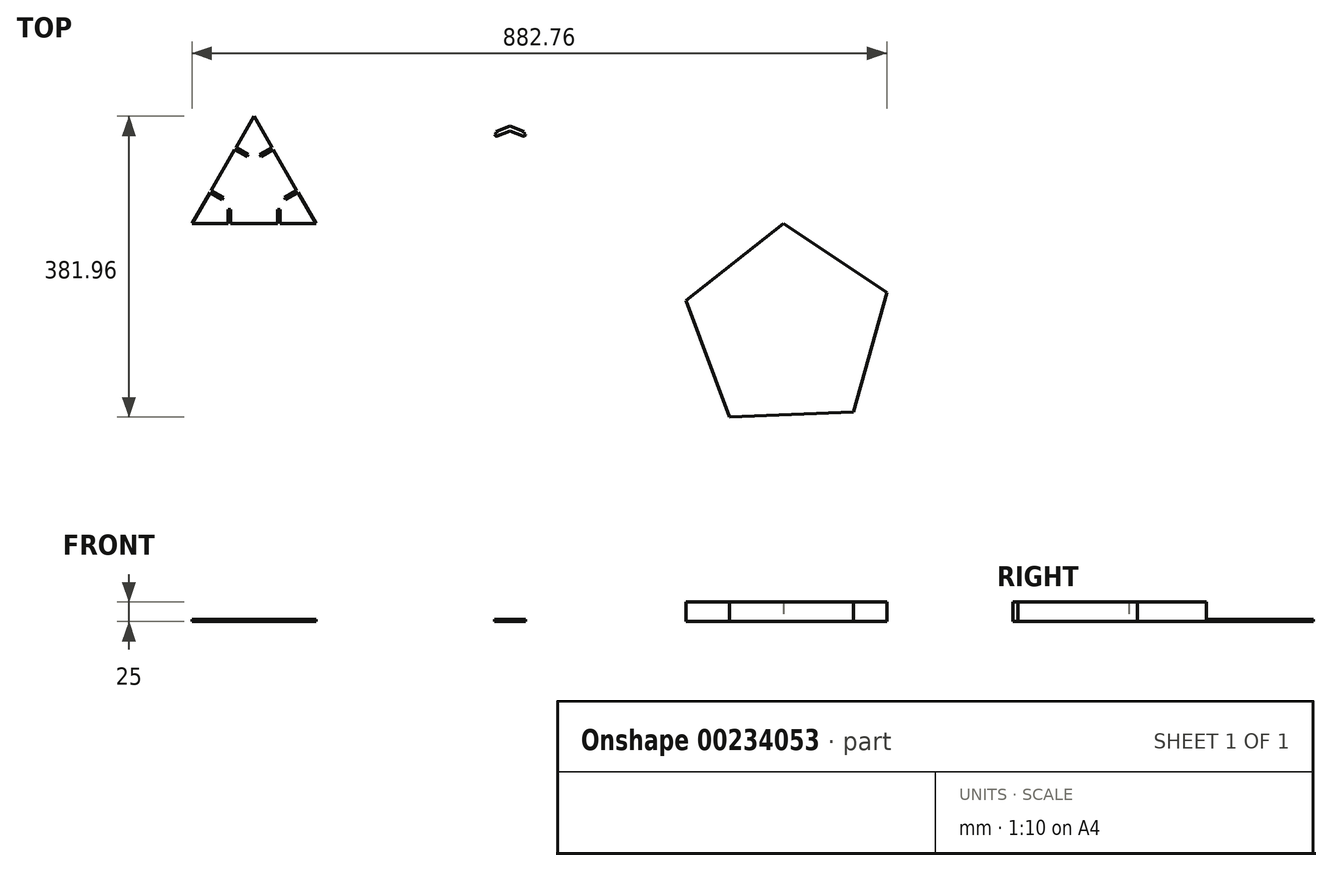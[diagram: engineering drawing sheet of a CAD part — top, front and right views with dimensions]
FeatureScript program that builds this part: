
annotation { "Feature Type Name" : "Feature", "Feature Type Description" : "" }
export const myFeature = defineFeature(function(context is Context, id is Id, definition is map)
    precondition{}
    {
        {
            var Q0;
            Q0=qCreatedBy(makeId("Top.planeOp"),FACE);
            var sketch = newSketch(context, id + "F0", { "sketchPlane" : qUnion([Q0])});
            skLineSegment(sketch, "E0", {"start": v(0, 0) * mm, "end": v(78.83, 136.53) * mm});
            skLineSegment(sketch, "E1", {"start": v(78.83, 136.53) * mm, "end": v(157.65, 0) * mm});
            skLineSegment(sketch, "E2", {"start": v(157.65, 0) * mm, "end": v(0, 0) * mm});
            skLineSegment(sketch, "E3", {"start": v(78.83, 136.53) * mm, "end": v(236.47, 136.53) * mm});
            skLineSegment(sketch, "E4", {"start": v(236.48, 136.53) * mm, "end": v(157.65, 0) * mm});
            skLineSegment(sketch, "E5", {"start": v(78.83, 136.53) * mm, "end": v(157.65, 273.06) * mm});
            skLineSegment(sketch, "E6", {"start": v(157.65, 273.06) * mm, "end": v(236.47, 136.53) * mm});
            skLineSegment(sketch, "E7.1.0", {"start": v(157.65, 0) * mm, "end": v(78.83, -136.53) * mm});
            skLineSegment(sketch, "E7.1.1", {"start": v(0, 0) * mm, "end": v(157.65, 0) * mm});
            skLineSegment(sketch, "E7.1.2", {"start": v(78.83, -136.53) * mm, "end": v(0, 0) * mm});
            skLineSegment(sketch, "E7.1.3", {"start": v(157.65, 0) * mm, "end": v(315.3, 0) * mm});
            skLineSegment(sketch, "E7.1.4", {"start": v(236.48, -136.53) * mm, "end": v(78.83, -136.53) * mm});
            skLineSegment(sketch, "E7.1.5", {"start": v(157.65, 0) * mm, "end": v(236.48, -136.53) * mm});
            skLineSegment(sketch, "E7.1.6", {"start": v(315.3, 0) * mm, "end": v(236.47, -136.53) * mm});
            skLineSegment(sketch, "E7.2.0", {"start": v(78.83, -136.53) * mm, "end": v(-78.82, -136.53) * mm});
            skLineSegment(sketch, "E7.2.1", {"start": v(0, 0) * mm, "end": v(78.83, -136.53) * mm});
            skLineSegment(sketch, "E7.2.2", {"start": v(-78.82, -136.53) * mm, "end": v(0, 0) * mm});
            skLineSegment(sketch, "E7.2.3", {"start": v(78.83, -136.53) * mm, "end": v(157.65, -273.06) * mm});
            skLineSegment(sketch, "E7.2.4", {"start": v(0, -273.06) * mm, "end": v(-78.83, -136.53) * mm});
            skLineSegment(sketch, "E7.2.5", {"start": v(78.83, -136.53) * mm, "end": v(0, -273.06) * mm});
            skLineSegment(sketch, "E7.2.6", {"start": v(157.65, -273.06) * mm, "end": v(0, -273.06) * mm});
            skLineSegment(sketch, "E7.3.0", {"start": v(-78.83, -136.53) * mm, "end": v(-157.65, 0) * mm});
            skLineSegment(sketch, "E7.3.1", {"start": v(0, 0) * mm, "end": v(-78.83, -136.53) * mm});
            skLineSegment(sketch, "E7.3.2", {"start": v(-157.65, 0) * mm, "end": v(0, 0) * mm});
            skLineSegment(sketch, "E7.3.3", {"start": v(-78.83, -136.53) * mm, "end": v(-157.65, -273.06) * mm});
            skLineSegment(sketch, "E7.3.4", {"start": v(-236.48, -136.53) * mm, "end": v(-157.65, 0) * mm});
            skLineSegment(sketch, "E7.3.5", {"start": v(-78.83, -136.53) * mm, "end": v(-236.47, -136.53) * mm});
            skLineSegment(sketch, "E7.3.6", {"start": v(-157.65, -273.06) * mm, "end": v(-236.47, -136.53) * mm});
            skLineSegment(sketch, "E7.4.0", {"start": v(-157.65, 0) * mm, "end": v(-78.83, 136.53) * mm});
            skLineSegment(sketch, "E7.4.1", {"start": v(0, 0) * mm, "end": v(-157.65, 0) * mm});
            skLineSegment(sketch, "E7.4.2", {"start": v(-78.83, 136.53) * mm, "end": v(0, 0) * mm});
            skLineSegment(sketch, "E7.4.3", {"start": v(-157.65, 0) * mm, "end": v(-315.3, 0) * mm});
            skLineSegment(sketch, "E7.4.4", {"start": v(-236.48, 136.53) * mm, "end": v(-78.83, 136.53) * mm});
            skLineSegment(sketch, "E7.4.5", {"start": v(-157.65, 0) * mm, "end": v(-236.48, 136.53) * mm});
            skLineSegment(sketch, "E7.4.6", {"start": v(-315.3, 0) * mm, "end": v(-236.47, 136.53) * mm});
            skPoint(sketch, "E7.center", {"position": v(0, 0) * mm});
            skLineSegment(sketch, "E7.anchor1", {"start": v(0, 0) * mm, "end": v(157.65, 0) * mm, "construction": true});
            skLineSegment(sketch, "E7.anchor2", {"start": v(0, 0) * mm, "end": v(-78.83, 136.53) * mm, "construction": true});
            skSolve(sketch);
        }
        {
            var Q0;
            Q0=qCreatedBy(makeId("Top.planeOp"),FACE);
            var sketch = newSketch(context, id + "F1", { "sketchPlane" : qUnion([Q0])});
            skLineSegment(sketch, "E8.0", {"start": v(0, 0) * mm, "end": v(78.83, 136.53) * mm});
            skLineSegment(sketch, "E8.1", {"start": v(78.83, 136.53) * mm, "end": v(157.65, 273.06) * mm});
            skLineSegment(sketch, "E8.2", {"start": v(157.65, 273.06) * mm, "end": v(236.47, 136.53) * mm});
            skLineSegment(sketch, "E8.3", {"start": v(236.48, 136.53) * mm, "end": v(157.65, 0) * mm});
            skLineSegment(sketch, "E8.4", {"start": v(157.65, 0) * mm, "end": v(315.3, 0) * mm});
            skLineSegment(sketch, "E9.0", {"start": v(315.3, 0) * mm, "end": v(236.47, -136.53) * mm});
            skLineSegment(sketch, "E10.0", {"start": v(236.48, -136.53) * mm, "end": v(78.83, -136.53) * mm});
            skLineSegment(sketch, "E11.0", {"start": v(78.83, -136.53) * mm, "end": v(157.65, -273.06) * mm});
            skLineSegment(sketch, "E12.0", {"start": v(157.65, -273.06) * mm, "end": v(0, -273.06) * mm});
            skLineSegment(sketch, "E13.0", {"start": v(0, -273.06) * mm, "end": v(-78.83, -136.53) * mm});
            skLineSegment(sketch, "E14.0", {"start": v(-78.83, -136.53) * mm, "end": v(-157.65, -273.06) * mm});
            skLineSegment(sketch, "E15.0", {"start": v(-157.65, -273.06) * mm, "end": v(-236.47, -136.53) * mm});
            skLineSegment(sketch, "E16.0", {"start": v(-236.48, -136.53) * mm, "end": v(-157.65, 0) * mm});
            skLineSegment(sketch, "E17.0", {"start": v(-157.65, 0) * mm, "end": v(-315.3, 0) * mm});
            skLineSegment(sketch, "E18.0", {"start": v(-315.3, 0) * mm, "end": v(-236.47, 136.53) * mm});
            skLineSegment(sketch, "E19.0", {"start": v(-236.48, 136.53) * mm, "end": v(-78.83, 136.53) * mm});
            skLineSegment(sketch, "E20.0", {"start": v(-78.83, 136.53) * mm, "end": v(0, 0) * mm});
            skSolve(sketch);
        }
        {
            var Q0;
            Q0=makeQuery(id+"F0.imprint","IMPRINT",FACE,{"disambiguationData":[TD([[makeQuery(id+"F0.imprint","IMPRINT",EDGE,{"derivedFrom":sQuery(id+"F0.wireOp",EDGE,"E0")}),-1.0]])]});
            extrude(context, id + "F2", {"entities" : qUnion([Q0]), "depth" : 3 * mm});
        }
        {
            var Q0;
            Q0=qCreatedBy(makeId("Top.planeOp"),FACE);
            var sketch = newSketch(context, id + "F3", { "sketchPlane" : qUnion([Q0])});
            skCircle(sketch, "E21.cCircle", {"center": v(757.04, -133.78) * mm, "radius": 108.5 * mm, "construction": true});
            skLineSegment(sketch, "E21.0", {"start": v(882.76, -87.12) * mm, "end": v(840.27, -238.93) * mm});
            skLineSegment(sketch, "E21.1", {"start": v(840.27, -238.93) * mm, "end": v(682.76, -245.43) * mm});
            skLineSegment(sketch, "E21.2", {"start": v(682.76, -245.43) * mm, "end": v(627.9, -97.64) * mm});
            skLineSegment(sketch, "E21.3", {"start": v(627.9, -97.64) * mm, "end": v(751.5, 0.2) * mm});
            skLineSegment(sketch, "E21.4", {"start": v(751.5, 0.2) * mm, "end": v(882.76, -87.12) * mm});
            skPoint(sketch, "E21.0.midPoint", {"position": v(861.52, -163.02) * mm});
            skSolve(sketch);
        }
        {
            var Q0;
            Q0 = qSketchRegion(id + "F3", true);
            extrude(context, id + "F4", {"entities" : qUnion([Q0]), "depth" : 25 * mm});
        }
        {
            var Q0;
            Q0=makeQuery(id+"F2.opExtrude","CAP_FACE",FACE,{"disambiguationData":[OSD([sQuery(id+"F0.wireOp",EDGE,"E0"),sQuery(id+"F0.wireOp",EDGE,"E1"),sQuery(id+"F0.wireOp",EDGE,"E7.1.1")])],"isStart":false});
            var sketch = newSketch(context, id + "F5", { "sketchPlane" : qUnion([Q0])});
            skLineSegment(sketch, "E22.0", {"start": v(0, 0) * mm, "end": v(78.83, 136.53) * mm, "construction": true});
            skLineSegment(sketch, "E23.0", {"start": v(78.83, 136.53) * mm, "end": v(157.65, 0) * mm, "construction": true});
            skPoint(sketch, "E24.0", {"position": v(78.83, 0) * mm});
            skLineSegment(sketch, "E25.0", {"start": v(0, 0) * mm, "end": v(157.65, 0) * mm, "construction": true});
            skPoint(sketch, "E26", {"position": v(39.41, 68.26) * mm});
            skPoint(sketch, "E27", {"position": v(118.24, 68.26) * mm});
            skLineSegment(sketch, "E28", {"start": v(48.83, 0) * mm, "end": v(48.83, 18) * mm});
            skLineSegment(sketch, "E29", {"start": v(48.83, 18) * mm, "end": v(45.83, 18) * mm});
            skLineSegment(sketch, "E30", {"start": v(45.83, 18) * mm, "end": v(45.83, 0) * mm});
            skLineSegment(sketch, "E31", {"start": v(45.83, 0) * mm, "end": v(48.83, 0) * mm});
            skLineSegment(sketch, "E32", {"start": v(111.83, 0) * mm, "end": v(111.83, 18) * mm});
            skLineSegment(sketch, "E33", {"start": v(111.83, 18) * mm, "end": v(108.83, 18) * mm});
            skLineSegment(sketch, "E34", {"start": v(108.83, 18) * mm, "end": v(108.83, 0) * mm});
            skLineSegment(sketch, "E35", {"start": v(108.83, 0) * mm, "end": v(111.83, 0) * mm});
            skLineSegment(sketch, "E36", {"start": v(40, 33.28) * mm, "end": v(24.41, 42.28) * mm});
            skLineSegment(sketch, "E37", {"start": v(24.41, 42.28) * mm, "end": v(22.91, 39.69) * mm});
            skLineSegment(sketch, "E38", {"start": v(22.91, 39.69) * mm, "end": v(38.5, 30.69) * mm});
            skLineSegment(sketch, "E39", {"start": v(38.5, 30.69) * mm, "end": v(40, 33.28) * mm});
            skLineSegment(sketch, "E40", {"start": v(71.5, 87.84) * mm, "end": v(55.91, 96.84) * mm});
            skLineSegment(sketch, "E41", {"start": v(55.91, 96.84) * mm, "end": v(54.41, 94.25) * mm});
            skLineSegment(sketch, "E42", {"start": v(54.41, 94.25) * mm, "end": v(70, 85.25) * mm});
            skLineSegment(sketch, "E43", {"start": v(70, 85.25) * mm, "end": v(71.5, 87.84) * mm});
            skLineSegment(sketch, "E44", {"start": v(101.74, 96.84) * mm, "end": v(86.15, 87.84) * mm});
            skLineSegment(sketch, "E45", {"start": v(86.15, 87.84) * mm, "end": v(87.65, 85.25) * mm});
            skLineSegment(sketch, "E46", {"start": v(87.65, 85.25) * mm, "end": v(103.24, 94.25) * mm});
            skLineSegment(sketch, "E47", {"start": v(103.24, 94.25) * mm, "end": v(101.74, 96.84) * mm});
            skLineSegment(sketch, "E48", {"start": v(133.24, 42.28) * mm, "end": v(117.65, 33.28) * mm});
            skLineSegment(sketch, "E49", {"start": v(117.65, 33.28) * mm, "end": v(119.15, 30.69) * mm});
            skLineSegment(sketch, "E50", {"start": v(119.15, 30.69) * mm, "end": v(134.74, 39.69) * mm});
            skLineSegment(sketch, "E51", {"start": v(134.74, 39.69) * mm, "end": v(133.24, 42.28) * mm});
            skSolve(sketch);
        }
        {
            var Q0;
            Q0 = qSketchRegion(id + "F5", true);
            extrude(context, id + "F6", {"entities" : qUnion([Q0]), "operationType" : NewBodyOperationType.REMOVE, "oppositeDirection" : true, "depth" : 25 * mm});
        }
        {
            var Q0;
            Q0=qCreatedBy(makeId("Top.planeOp"),FACE);
            var sketch = newSketch(context, id + "F7", { "sketchPlane" : qUnion([Q0])});
            skLineSegment(sketch, "E52", {"start": v(404.23, 132.2) * mm, "end": v(404.23, 110.87) * mm, "construction": true});
            skLineSegment(sketch, "E53", {"start": v(404.23, 124.16) * mm, "end": v(386.35, 117.33) * mm});
            skLineSegment(sketch, "E54", {"start": v(386.35, 117.33) * mm, "end": v(387.42, 114.53) * mm});
            skLineSegment(sketch, "E55", {"start": v(387.42, 114.53) * mm, "end": v(384.62, 113.46) * mm});
            skLineSegment(sketch, "E56", {"start": v(384.62, 113.46) * mm, "end": v(384.97, 112.52) * mm});
            skLineSegment(sketch, "E57", {"start": v(387.56, 111.37) * mm, "end": v(404.23, 117.74) * mm});
            skLineSegment(sketch, "E58", {"start": v(387.42, 114.53) * mm, "end": v(404.23, 120.95) * mm, "construction": true});
            skPoint(sketch, "E59.visualSharp", {"position": v(385.69, 110.66) * mm});
            skArc(sketch, "E59.filletArc", {"start": v(384.97, 112.52) * mm, "mid": v(386.03, 111.41) * mm, "end": v(387.56, 111.37) * mm});
            skLineSegment(sketch, "E60.MirrorCS", {"start": v(423.85, 113.46) * mm, "end": v(423.5, 112.52) * mm});
            skArc(sketch, "E61.MirrorCS", {"start": v(423.5, 112.52) * mm, "mid": v(422.44, 111.41) * mm, "end": v(420.91, 111.37) * mm});
            skLineSegment(sketch, "E62.MirrorCS", {"start": v(421.05, 114.53) * mm, "end": v(404.23, 120.95) * mm, "construction": true});
            skLineSegment(sketch, "E63.MirrorCS", {"start": v(404.23, 124.16) * mm, "end": v(422.12, 117.33) * mm});
            skLineSegment(sketch, "E64.MirrorCS", {"start": v(422.12, 117.33) * mm, "end": v(421.05, 114.53) * mm});
            skLineSegment(sketch, "E65.MirrorCS", {"start": v(420.91, 111.37) * mm, "end": v(404.23, 117.74) * mm});
            skLineSegment(sketch, "E66.MirrorCS", {"start": v(421.05, 114.53) * mm, "end": v(423.85, 113.46) * mm});
            skPoint(sketch, "E67.MirrorP", {"position": v(422.78, 110.66) * mm});
            skSolve(sketch);
        }
        {
            var Q0;
            Q0 = qSketchRegion(id + "F7", true);
            extrude(context, id + "F8", {"entities" : qUnion([Q0]), "depth" : 3 * mm});
        }
    });
